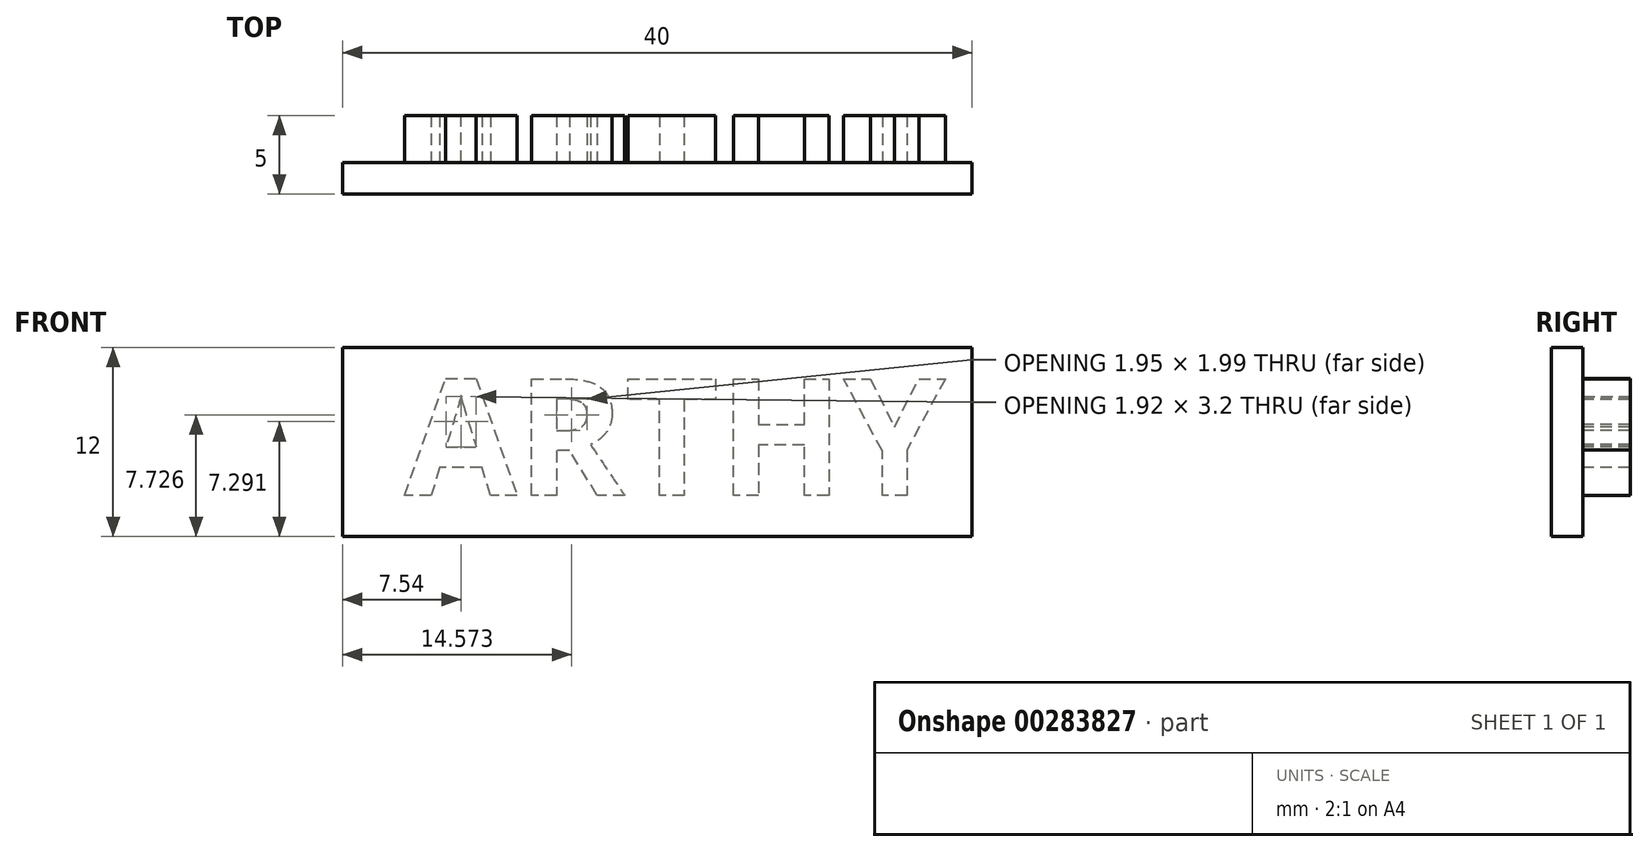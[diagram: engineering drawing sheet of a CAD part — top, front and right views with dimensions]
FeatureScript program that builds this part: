
annotation { "Feature Type Name" : "Feature", "Feature Type Description" : "" }
export const myFeature = defineFeature(function(context is Context, id is Id, definition is map)
    precondition{}
    {
        {
            var Q0;
            Q0=qCreatedBy(makeId("Front.planeOp"),FACE);
            var sketch = newSketch(context, id + "F0", { "sketchPlane" : qUnion([Q0])});
            skText(sketch, "E0", { "text": "ARTHY", "fontName": "OpenSans-Bold.ttf"});
            const initialGuessF0  = {"E0": [-0.018, -0.00392, 1, 0, 0.00745]};
            skSetInitialGuess(sketch, initialGuessF0);
            skSolve(sketch);
        }
        {
            var Q0;
            Q0 = qSketchRegion(id + "F0", true);
            extrude(context, id + "F1", {"entities" : qUnion([Q0]), "oppositeDirection" : true, "depth" : 3 * mm});
        }
        {
            var Q0;
            Q0=qCreatedBy(makeId("Front.planeOp"),FACE);
            var sketch = newSketch(context, id + "F2", { "sketchPlane" : qUnion([Q0])});
            skLineSegment(sketch, "E1.bottom", {"start": v(-21.96, 5.46) * mm, "end": v(18.04, 5.46) * mm});
            skLineSegment(sketch, "E1.top", {"start": v(-21.96, -6.54) * mm, "end": v(18.04, -6.54) * mm});
            skLineSegment(sketch, "E1.left", {"start": v(-21.96, 5.46) * mm, "end": v(-21.96, -6.54) * mm});
            skLineSegment(sketch, "E1.right", {"start": v(18.04, 5.46) * mm, "end": v(18.04, -6.54) * mm});
            skSolve(sketch);
        }
        {
            var Q0;
            Q0 = qSketchRegion(id + "F2", true);
            extrude(context, id + "F3", {"entities" : qUnion([Q0]), "depth" : 2 * mm});
        }
    });
